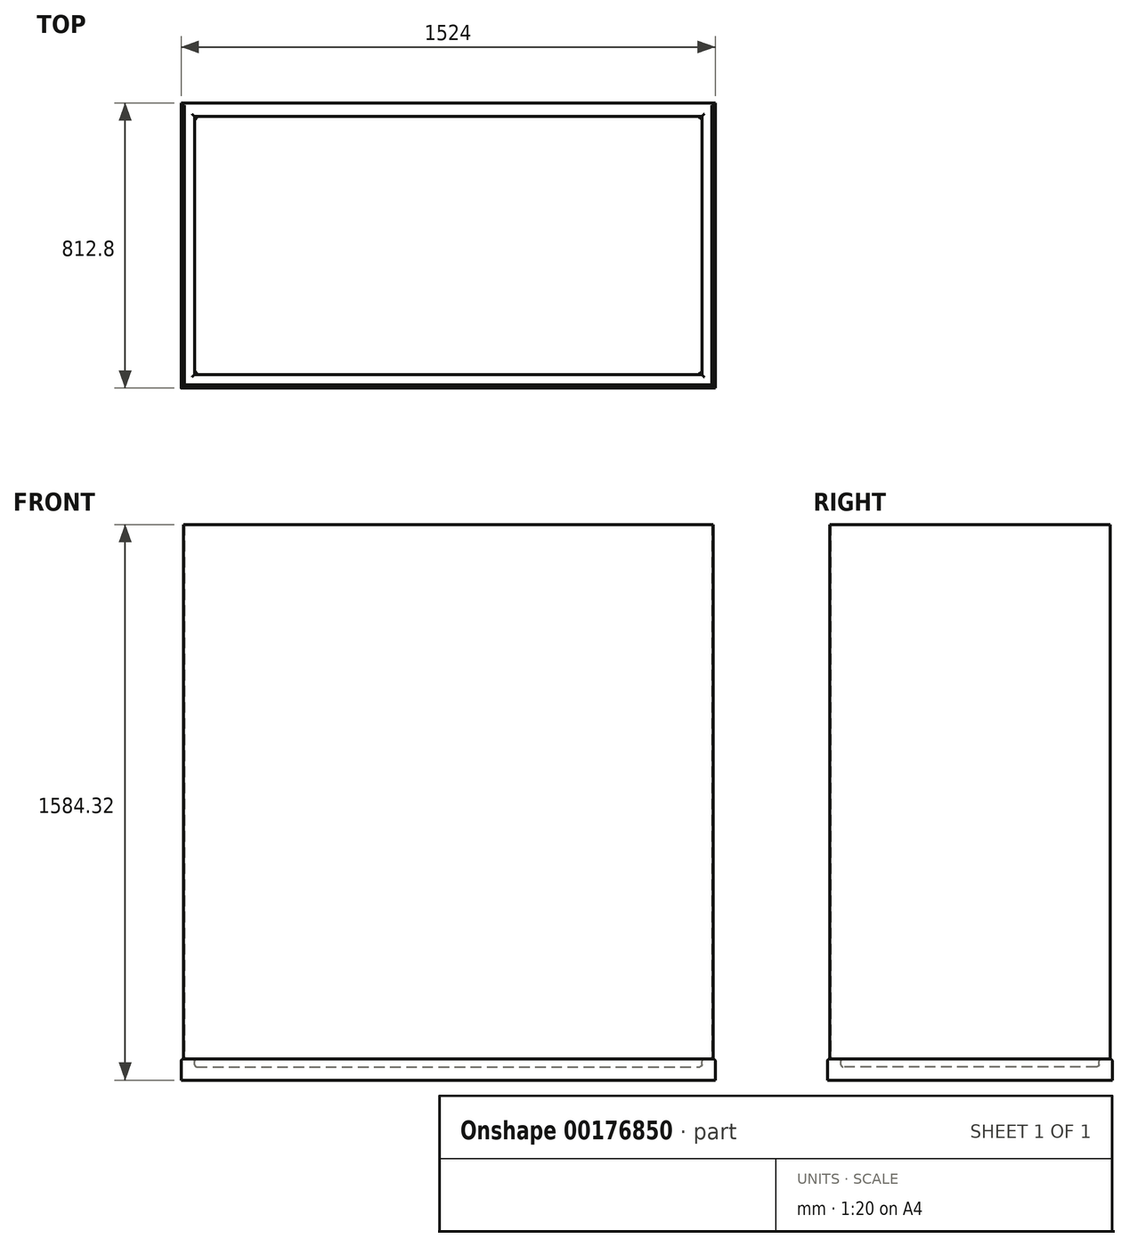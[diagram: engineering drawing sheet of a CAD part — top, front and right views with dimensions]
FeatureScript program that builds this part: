
annotation { "Feature Type Name" : "Feature", "Feature Type Description" : "" }
export const myFeature = defineFeature(function(context is Context, id is Id, definition is map)
    precondition{}
    {
        {
            var Q0;
            Q0=qCreatedBy(makeId("Top.planeOp"),FACE);
            var sketch = newSketch(context, id + "F0", { "sketchPlane" : qUnion([Q0])});
            skLineSegment(sketch, "E0.bottom", {"start": v(-770.1, -57.13) * mm, "end": v(753.9, -57.13) * mm});
            skLineSegment(sketch, "E0.top", {"start": v(-770.1, -869.93) * mm, "end": v(753.9, -869.93) * mm});
            skLineSegment(sketch, "E0.left", {"start": v(-770.1, -57.13) * mm, "end": v(-770.1, -869.93) * mm});
            skLineSegment(sketch, "E0.right", {"start": v(753.9, -57.13) * mm, "end": v(753.9, -869.93) * mm});
            skSolve(sketch);
        }
        {
            var Q0;
            Q0=makeQuery(id+"F0.imprint","IMPRINT",FACE,{"disambiguationData":[TD([[makeQuery(id+"F0.imprint","IMPRINT",EDGE,{"derivedFrom":sQuery(id+"F0.wireOp",EDGE,"E0.bottom")}),-1.0]])]});
            extrude(context, id + "F1", {"entities" : qUnion([Q0]), "oppositeDirection" : true, "depth" : 60.32 * mm});
        }
        {
            var Q0;
            Q0=makeQuery(id+"F1.opExtrude","CAP_FACE",FACE,{"disambiguationData":[OSD([sQuery(id+"F0.wireOp",EDGE,"E0.bottom"),sQuery(id+"F0.wireOp",EDGE,"E0.top"),sQuery(id+"F0.wireOp",EDGE,"E0.left"),sQuery(id+"F0.wireOp",EDGE,"E0.right")])],"isStart":true});
            shell(context, id + "F2", {"entities" : qUnion([Q0]), "thickness" : 38.1 * mm});
        }
        {
            var Q0;
            {var subQ0=sQuery(id+"F0.wireOp",EDGE,"E0.left");Q0=makeQuery(id+"F2.opShell","OFFSET_EDGE",EDGE,{"disambiguationData":[OSD([subQ0]),TDD([makeQuery(id+"F1.opExtrude","CAP_EDGE",EDGE,{"disambiguationData":[OSD([subQ0])],"isStart":true})])]});}
            var Q1;
            Q1=makeQuery(id+"F1.opExtrude","CAP_FACE",FACE,{"disambiguationData":[OSD([sQuery(id+"F0.wireOp",EDGE,"E0.bottom"),sQuery(id+"F0.wireOp",EDGE,"E0.top"),sQuery(id+"F0.wireOp",EDGE,"E0.left"),sQuery(id+"F0.wireOp",EDGE,"E0.right")])],"isStart":true});
            var Q2;
            {var subQ0=sQuery(id+"F0.wireOp",EDGE,"E0.bottom");Q2=makeQuery(id+"F2.opShell","OFFSET_EDGE",EDGE,{"disambiguationData":[OSD([subQ0]),TDD([makeQuery(id+"F1.opExtrude","CAP_EDGE",EDGE,{"disambiguationData":[OSD([subQ0])],"isStart":false})])]});}
            var Q3;
            {var subQ0=sQuery(id+"F0.wireOp",EDGE,"E0.left");Q3=makeQuery(id+"F2.opShell","OFFSET_EDGE",EDGE,{"disambiguationData":[OSD([subQ0]),TDD([makeQuery(id+"F1.opExtrude","CAP_EDGE",EDGE,{"disambiguationData":[OSD([subQ0])],"isStart":false})])]});}
            var Q4;
            {var subQ0=sQuery(id+"F0.wireOp",EDGE,"E0.right");Q4=makeQuery(id+"F2.opShell","OFFSET_EDGE",EDGE,{"disambiguationData":[OSD([subQ0]),TDD([makeQuery(id+"F1.opExtrude","CAP_EDGE",EDGE,{"disambiguationData":[OSD([subQ0])],"isStart":false})])]});}
            var Q5;
            {var subQ0=sQuery(id+"F0.wireOp",EDGE,"E0.top");Q5=makeQuery(id+"F2.opShell","OFFSET_EDGE",EDGE,{"disambiguationData":[OSD([subQ0]),TDD([makeQuery(id+"F1.opExtrude","CAP_EDGE",EDGE,{"disambiguationData":[OSD([subQ0])],"isStart":false})])]});}
            fillet(context, id + "F3", {"entities" : qUnion([Q0, Q1, Q2, Q3, Q4, Q5]), "radius" : 6.35 * mm, "tangentPropagation" : true, "allowEdgeOverflow" : false});
        }
        {
            var Q0;
            Q0=makeQuery(id+"F1.opExtrude","CAP_FACE",FACE,{"disambiguationData":[OSD([sQuery(id+"F0.wireOp",EDGE,"E0.bottom"),sQuery(id+"F0.wireOp",EDGE,"E0.top"),sQuery(id+"F0.wireOp",EDGE,"E0.left"),sQuery(id+"F0.wireOp",EDGE,"E0.right")])],"isStart":true});
            var sketch = newSketch(context, id + "F4", { "sketchPlane" : qUnion([Q0])});
            skLineSegment(sketch, "E1", {"start": v(-763.74, -63.48) * mm, "end": v(-763.74, -863.58) * mm});
            skLineSegment(sketch, "E2", {"start": v(-763.74, -863.58) * mm, "end": v(747.56, -863.58) * mm});
            skLineSegment(sketch, "E3", {"start": v(747.56, -863.58) * mm, "end": v(747.56, -63.48) * mm});
            skLineSegment(sketch, "E4.0", {"start": v(744.38, -860.4) * mm, "end": v(744.38, -63.48) * mm});
            skLineSegment(sketch, "E4.1", {"start": v(-760.57, -860.4) * mm, "end": v(744.38, -860.4) * mm});
            skLineSegment(sketch, "E4.2", {"start": v(-760.57, -63.48) * mm, "end": v(-760.57, -860.4) * mm});
            skLineSegment(sketch, "E5", {"start": v(-763.74, -63.48) * mm, "end": v(-760.57, -63.48) * mm});
            skLineSegment(sketch, "E6", {"start": v(744.38, -63.48) * mm, "end": v(747.56, -63.48) * mm});
            skSolve(sketch);
        }
        {
            var Q0;
            Q0=qSketchRegion(id+"F4",true);
            extrude(context, id + "F5", {"entities" : qUnion([Q0]), "depth" : 1524 * mm});
        }
    });
